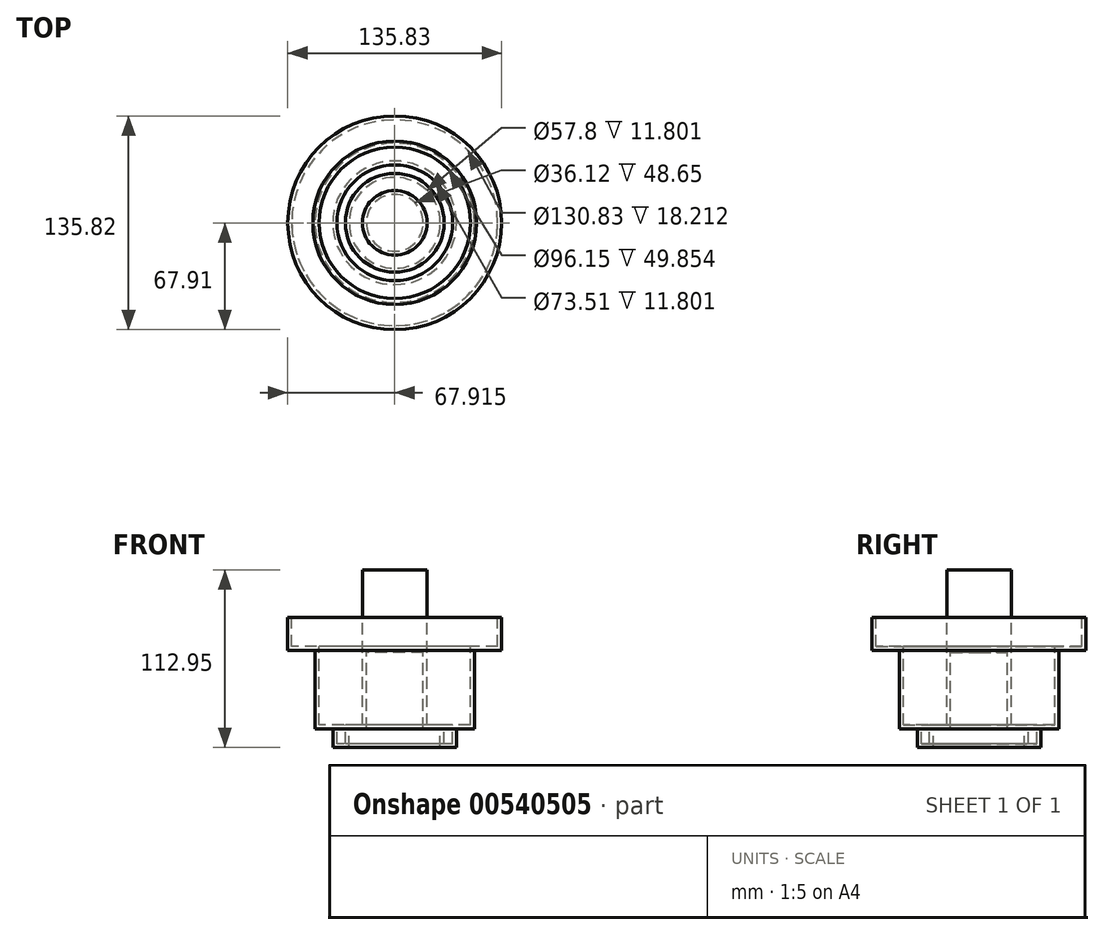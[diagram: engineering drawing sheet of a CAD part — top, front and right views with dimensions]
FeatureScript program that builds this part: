
annotation { "Feature Type Name" : "Feature", "Feature Type Description" : "" }
export const myFeature = defineFeature(function(context is Context, id is Id, definition is map)
    precondition{}
    {
        {
            var Q0;
            Q0=qCreatedBy(makeId("Front.planeOp"),FACE);
            var sketch = newSketch(context, id + "F0", { "sketchPlane" : qUnion([Q0])});
            skLineSegment(sketch, "E0", {"start": v(-30.07, 38.77) * mm, "end": v(21.94, 38.77) * mm});
            skLineSegment(sketch, "E1", {"start": v(21.94, 38.77) * mm, "end": v(21.94, 16.86) * mm});
            skLineSegment(sketch, "E2", {"start": v(21.94, 16.86) * mm, "end": v(3.88, 16.86) * mm});
            skLineSegment(sketch, "E3", {"start": v(3.88, 16.86) * mm, "end": v(3.88, -31.8) * mm});
            skLineSegment(sketch, "E4", {"start": v(3.88, -31.8) * mm, "end": v(-6.95, -31.8) * mm});
            skLineSegment(sketch, "E5", {"start": v(-6.95, -31.8) * mm, "end": v(-6.95, -43.6) * mm});
            skLineSegment(sketch, "E6", {"start": v(-6.95, -43.6) * mm, "end": v(-17.3, -43.6) * mm});
            skLineSegment(sketch, "E7", {"start": v(-17.3, -43.6) * mm, "end": v(-17.3, -31.8) * mm});
            skLineSegment(sketch, "E8", {"start": v(-17.3, -31.8) * mm, "end": v(-28.63, -31.8) * mm});
            skLineSegment(sketch, "E9", {"start": v(-28.63, -31.8) * mm, "end": v(-28.63, 18.06) * mm});
            skLineSegment(sketch, "E10", {"start": v(-28.63, 18.06) * mm, "end": v(-45.97, 18.06) * mm});
            skLineSegment(sketch, "E11", {"start": v(-45.97, 18.06) * mm, "end": v(-45.97, 39.26) * mm});
            skLineSegment(sketch, "E12", {"start": v(-45.97, 39.26) * mm, "end": v(-30.07, 38.77) * mm});
            skSolve(sketch);
        }
        {
            var Q0;
            Q0 = qSketchRegion(id + "F0", true);
            var Q1;
            Q1=sQuery(id+"F0.wireOp",EDGE,"E1");
            revolve(context, id + "F1", {"entities" : qUnion([Q0]), "axis" : qUnion([Q1]), "revolveType" : RevolveType.FULL});
        }
        {
            var Q0;
            Q0=makeQuery(id+"F1.opRevolve","SWEPT_FACE",FACE,{"disambiguationData":[OSD([sQuery(id+"F0.wireOp",EDGE,"E0")])]});
            shell(context, id + "F2", {"entities" : qUnion([Q0]), "thickness" : 2.5 * mm});
        }
        {
            var Q0;
            Q0=makeQuery(id+"F2.opShell","OFFSET_FACE",FACE,{"disambiguationData":[OSD([sQuery(id+"F0.wireOp",EDGE,"E2")])]});
            extrude(context, id + "F3", {"entities" : qUnion([Q0]), "operationType" : NewBodyOperationType.ADD, "depth" : 25 * mm, "offsetDistance" : 25 * mm});
        }
        {
            var Q0;
            Q0=makeQuery(id+"F3.opExtrude","CAP_FACE",FACE,{"disambiguationData":[OSD([sQuery(id+"F0.wireOp",EDGE,"E2")])],"isStart":false});
            extrude(context, id + "F4", {"entities" : qUnion([Q0]), "operationType" : NewBodyOperationType.ADD, "depth" : 25 * mm, "offsetDistance" : 25 * mm});
        }
    });
